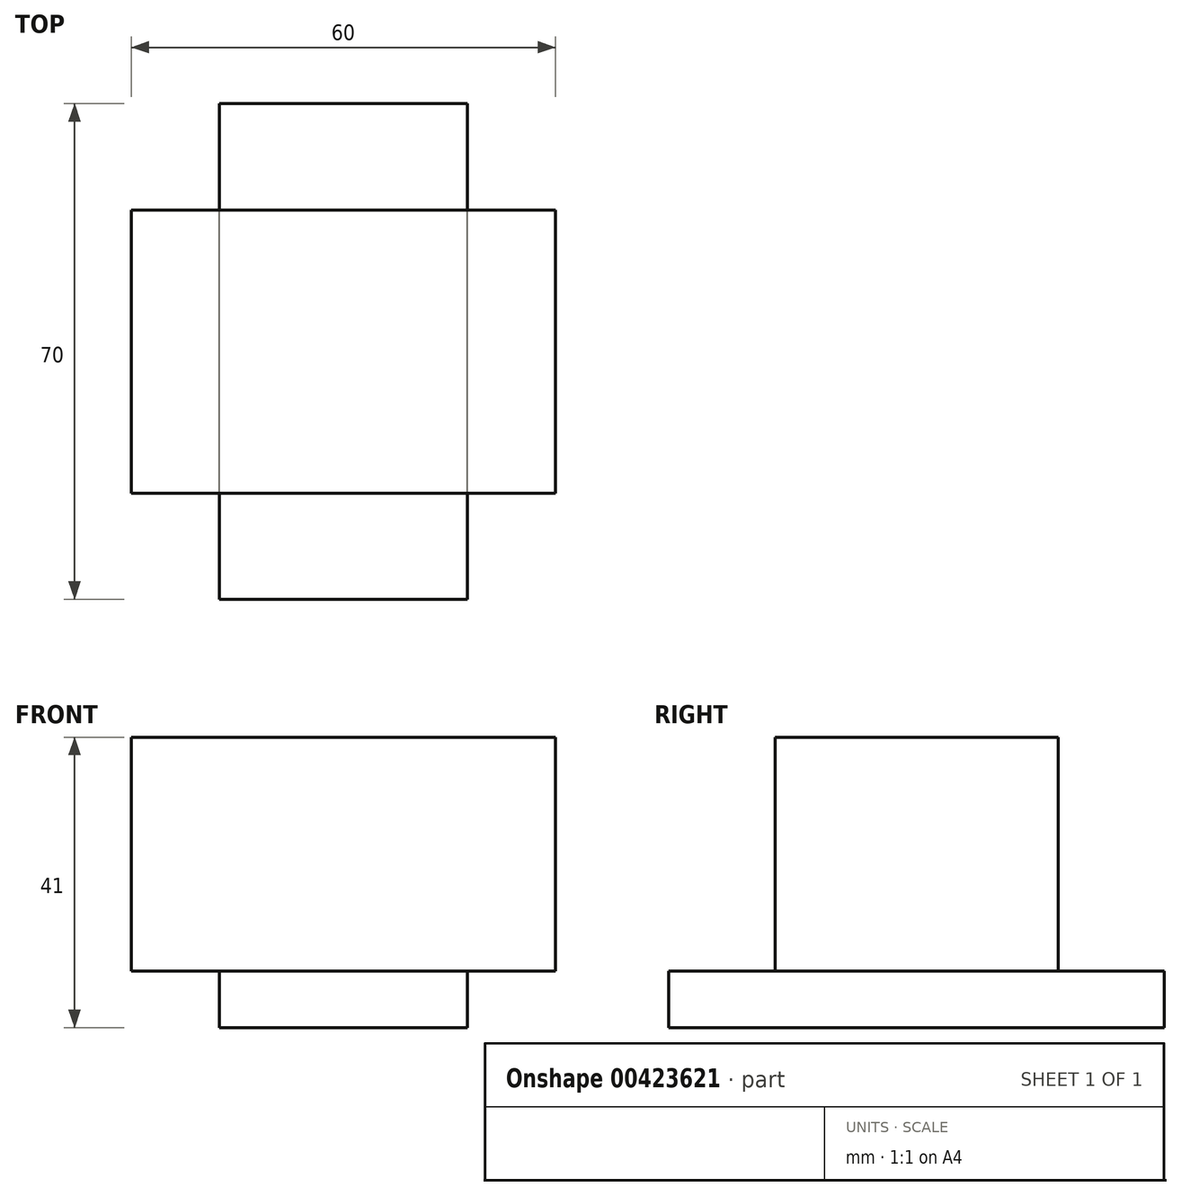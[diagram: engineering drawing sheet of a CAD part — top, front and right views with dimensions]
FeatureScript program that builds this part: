
annotation { "Feature Type Name" : "Feature", "Feature Type Description" : "" }
export const myFeature = defineFeature(function(context is Context, id is Id, definition is map)
    precondition{}
    {
        {
            var Q0;
            Q0=qCreatedBy(makeId("Front.planeOp"),FACE);
            var sketch = newSketch(context, id + "F0", { "sketchPlane" : qUnion([Q0])});
            skLineSegment(sketch, "E0.bottom", {"start": v(-17.5, 8) * mm, "end": v(17.5, 8) * mm});
            skLineSegment(sketch, "E0.top", {"start": v(-17.5, 0) * mm, "end": v(17.5, 0) * mm});
            skLineSegment(sketch, "E0.left", {"start": v(-17.5, 8) * mm, "end": v(-17.5, 0) * mm});
            skLineSegment(sketch, "E0.right", {"start": v(17.5, 8) * mm, "end": v(17.5, 0) * mm});
            skLineSegment(sketch, "E1.bottom", {"start": v(-30, 8) * mm, "end": v(30, 8) * mm});
            skLineSegment(sketch, "E1.top", {"start": v(-30, 41) * mm, "end": v(30, 41) * mm});
            skLineSegment(sketch, "E1.left", {"start": v(-30, 8) * mm, "end": v(-30, 41) * mm});
            skLineSegment(sketch, "E1.right", {"start": v(30, 8) * mm, "end": v(30, 41) * mm});
            skSolve(sketch);
        }
        {
            var Q0;
            Q0=makeQuery(id+"F0.imprint","IMPRINT",FACE,{"disambiguationData":[TD([[makeQuery(id+"F0.imprint","IMPRINT",EDGE,{"derivedFrom":sQuery(id+"F0.wireOp",EDGE,"E0.bottom")}),-1.0]])]});
            var Q1;
            Q1=makeQuery(id+"F0.imprint","IMPRINT",FACE,{"disambiguationData":[TD([[makeQuery(id+"F0.imprint","IMPRINT",EDGE,{"derivedFrom":sQuery(id+"F0.wireOp",EDGE,"E0.top")}),1.0]])]});
            extrude(context, id + "F1", {"entities" : qUnion([Q0, Q1]), "endBound" : BoundingType.SYMMETRIC, "depth" : 70 * mm});
        }
        {
            var Q0;
            Q0 = qSketchRegion(id + "F0", true);
            extrude(context, id + "F2", {"entities" : qUnion([Q0]), "operationType" : NewBodyOperationType.ADD, "endBound" : BoundingType.SYMMETRIC, "depth" : 40 * mm});
        }
    });
